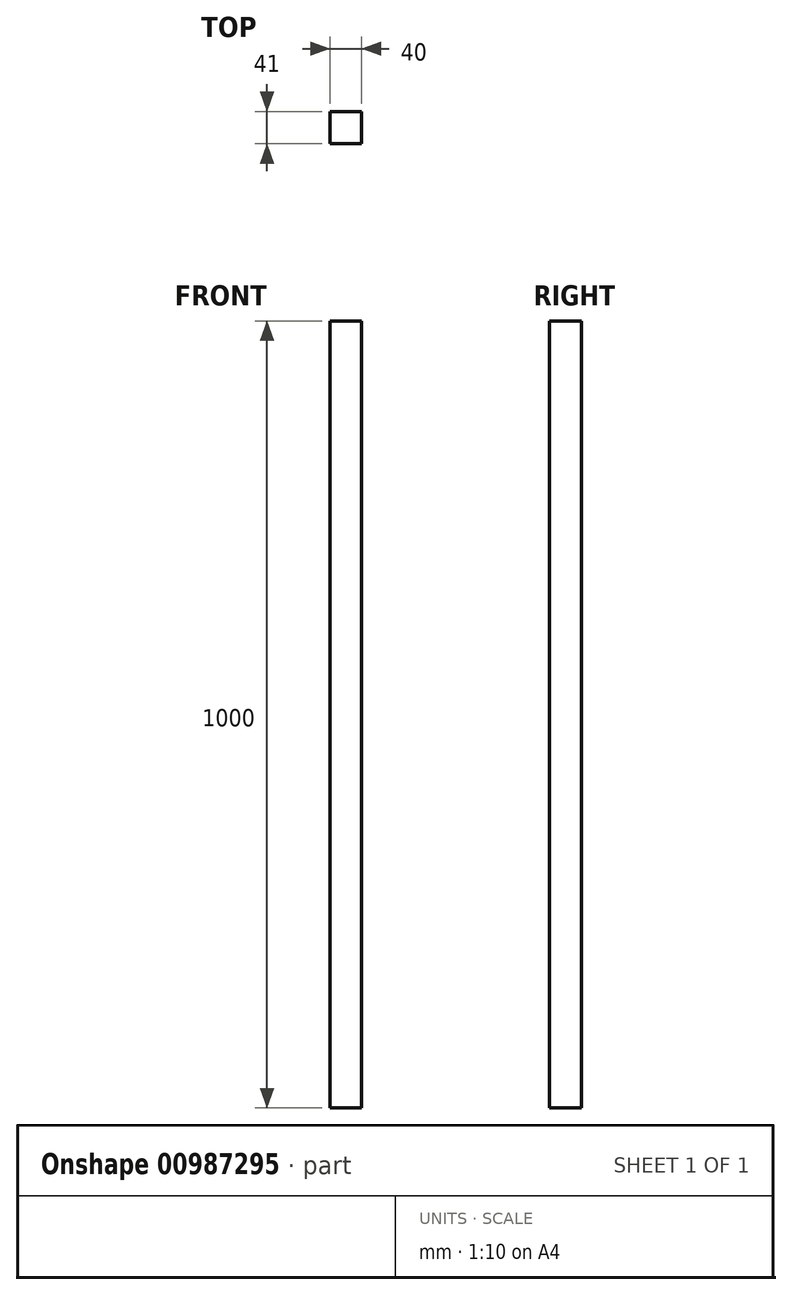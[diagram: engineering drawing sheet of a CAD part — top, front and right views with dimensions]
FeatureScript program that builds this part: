
annotation { "Feature Type Name" : "Feature", "Feature Type Description" : "" }
export const myFeature = defineFeature(function(context is Context, id is Id, definition is map)
    precondition{}
    {
        {
            var Q0;
            Q0=qCreatedBy(makeId("Front.planeOp"),FACE);
            var sketch = newSketch(context, id + "F0", { "sketchPlane" : qUnion([Q0])});
            skLineSegment(sketch, "E0.bottom", {"start": v(-21.43, 0) * mm, "end": v(18.57, 0) * mm});
            skLineSegment(sketch, "E0.top", {"start": v(-21.43, 1000) * mm, "end": v(18.57, 1000) * mm});
            skLineSegment(sketch, "E0.left", {"start": v(-21.43, 0) * mm, "end": v(-21.43, 1000) * mm});
            skLineSegment(sketch, "E0.right", {"start": v(18.57, 0) * mm, "end": v(18.57, 1000) * mm});
            skSolve(sketch);
        }
        {
            var Q0;
            Q0=makeQuery(id+"F0.imprint","IMPRINT",FACE,{"disambiguationData":[TD([[makeQuery(id+"F0.imprint","IMPRINT",EDGE,{"derivedFrom":sQuery(id+"F0.wireOp",EDGE,"E0.bottom")}),1.0]])]});
            extrude(context, id + "F1", {"entities" : qUnion([Q0]), "depth" : 41 * mm, "offsetDistance" : 25 * mm});
        }
    });
